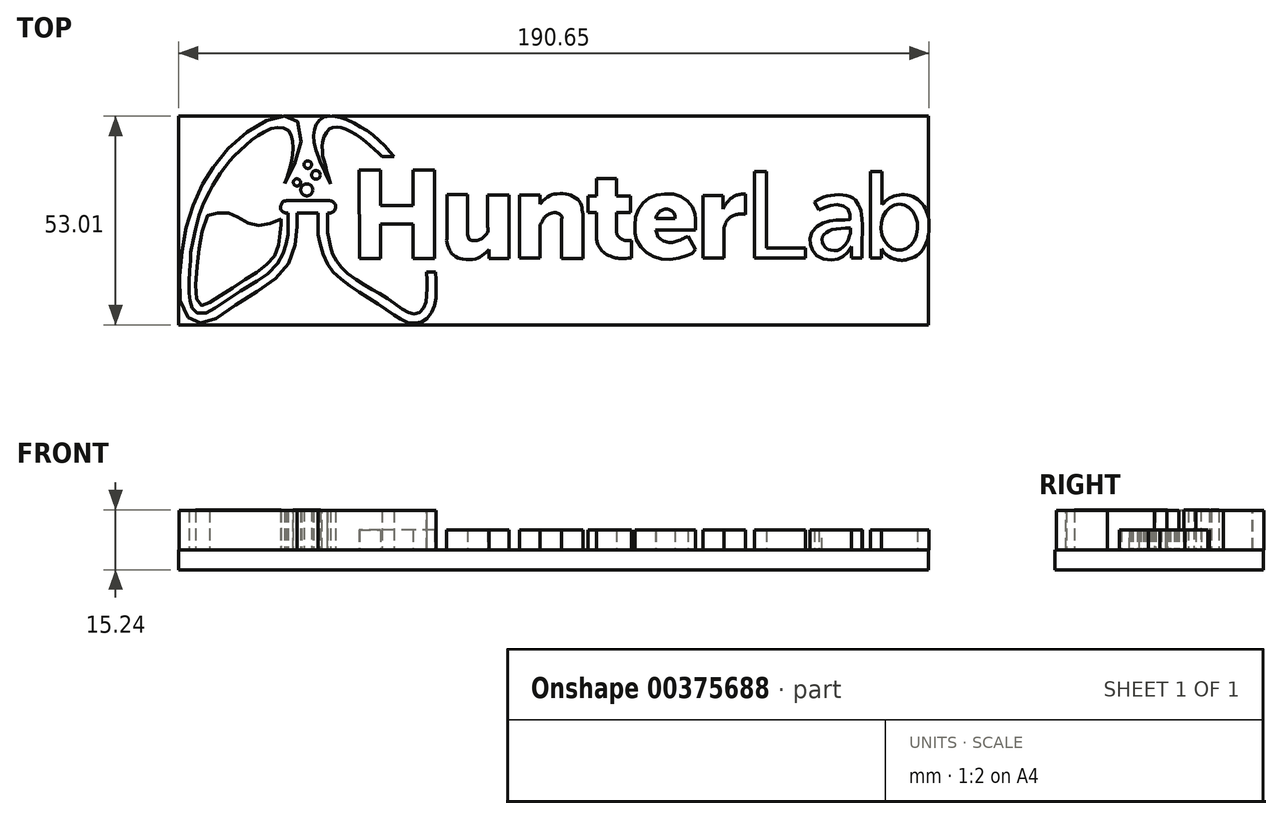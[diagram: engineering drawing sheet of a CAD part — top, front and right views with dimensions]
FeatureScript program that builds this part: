
annotation { "Feature Type Name" : "Feature", "Feature Type Description" : "" }
export const myFeature = defineFeature(function(context is Context, id is Id, definition is map)
    precondition{}
    {
        {
            var Q0;
            Q0=qCreatedBy(makeId("Top.planeOp"),FACE);
            var sketch = newSketch(context, id + "F0", { "sketchPlane" : qUnion([Q0])});
            skLineSegment(sketch, "E0.bottom", {"start": v(-95.8, -13.92) * mm, "end": v(94.76, -13.92) * mm});
            skLineSegment(sketch, "E0.top", {"start": v(-95.8, 39.08) * mm, "end": v(94.76, 39.08) * mm});
            skLineSegment(sketch, "E0.left", {"start": v(-95.8, -13.92) * mm, "end": v(-95.8, 39.08) * mm});
            skLineSegment(sketch, "E0.right", {"start": v(94.76, -13.92) * mm, "end": v(94.76, 39.08) * mm});
            skSolve(sketch);
        }
        {
            var Q0;
            Q0=qSketchRegion(id+"F0",true);
            extrude(context, id + "F1", {"entities" : qUnion([Q0]), "oppositeDirection" : true, "depth" : 5.08 * mm});
        }
        {
            var Q0;
            Q0=qCreatedBy(makeId("Top.planeOp"),FACE);
            var sketch = newSketch(context, id + "F2", { "sketchPlane" : qUnion([Q0])});
            skLineSegment(sketch, "E1", {"start": v(-49.96, 25.38) * mm, "end": v(-44.45, 25.38) * mm});
            skLineSegment(sketch, "E2", {"start": v(-44.45, 25.38) * mm, "end": v(-44.45, 16.38) * mm});
            skLineSegment(sketch, "E3", {"start": v(-44.45, 16.38) * mm, "end": v(-36.19, 16.38) * mm});
            skLineSegment(sketch, "E4", {"start": v(-36.19, 16.38) * mm, "end": v(-36.19, 25.38) * mm});
            skLineSegment(sketch, "E5", {"start": v(-36.19, 25.38) * mm, "end": v(-30.8, 25.38) * mm});
            skLineSegment(sketch, "E6", {"start": v(-30.8, 25.38) * mm, "end": v(-30.8, 2.94) * mm});
            skLineSegment(sketch, "E7", {"start": v(-30.8, 2.94) * mm, "end": v(-36.19, 2.94) * mm});
            skLineSegment(sketch, "E8", {"start": v(-36.19, 2.94) * mm, "end": v(-36.19, 11.68) * mm});
            skLineSegment(sketch, "E9", {"start": v(-36.19, 11.68) * mm, "end": v(-44.45, 11.68) * mm});
            skLineSegment(sketch, "E10", {"start": v(-44.45, 11.68) * mm, "end": v(-44.45, 2.94) * mm});
            skLineSegment(sketch, "E11", {"start": v(-44.45, 2.94) * mm, "end": v(-49.84, 2.94) * mm});
            skLineSegment(sketch, "E12", {"start": v(-49.84, 2.94) * mm, "end": v(-49.96, 25.38) * mm});
            skLineSegment(sketch, "E13", {"start": v(-22.34, 19.15) * mm, "end": v(-27.62, 19.15) * mm});
            skLineSegment(sketch, "E14", {"start": v(-27.62, 19.15) * mm, "end": v(-27.62, 7.97) * mm});
            skLineSegment(sketch, "E15", {"start": v(-22.34, 19.15) * mm, "end": v(-22.34, 9.02) * mm});
            skLineSegment(sketch, "E16", {"start": v(-17.24, 10.98) * mm, "end": v(-17.24, 19.09) * mm});
            skLineSegment(sketch, "E17", {"start": v(-17.24, 19.09) * mm, "end": v(-11.9, 19.09) * mm});
            skLineSegment(sketch, "E18", {"start": v(-11.9, 19.09) * mm, "end": v(-11.9, 2.93) * mm});
            skLineSegment(sketch, "E19", {"start": v(-11.9, 2.93) * mm, "end": v(-16.94, 2.93) * mm});
            skLineSegment(sketch, "E20", {"start": v(-16.94, 2.93) * mm, "end": v(-16.94, 5.2) * mm});
            skLineSegment(sketch, "E21", {"start": v(-3.91, 16.75) * mm, "end": v(-3.91, 19.03) * mm});
            skLineSegment(sketch, "E22", {"start": v(-3.91, 19.03) * mm, "end": v(-9.13, 19.03) * mm});
            skLineSegment(sketch, "E23", {"start": v(-9.13, 19.03) * mm, "end": v(-9.13, 3) * mm});
            skLineSegment(sketch, "E24", {"start": v(-9.13, 3) * mm, "end": v(-3.91, 3) * mm});
            skLineSegment(sketch, "E25", {"start": v(-3.91, 3) * mm, "end": v(-3.91, 11.53) * mm});
            skLineSegment(sketch, "E26", {"start": v(1.55, 12.95) * mm, "end": v(1.55, 2.93) * mm});
            skLineSegment(sketch, "E27", {"start": v(1.55, 2.93) * mm, "end": v(6.9, 2.93) * mm});
            skLineSegment(sketch, "E28", {"start": v(6.9, 2.93) * mm, "end": v(6.9, 14.18) * mm});
            skLineSegment(sketch, "E29", {"start": v(15.5, 9.36) * mm, "end": v(15.5, 14.66) * mm});
            skLineSegment(sketch, "E30", {"start": v(15.5, 14.66) * mm, "end": v(19, 14.66) * mm});
            skLineSegment(sketch, "E31", {"start": v(19, 14.66) * mm, "end": v(19, 18.73) * mm});
            skLineSegment(sketch, "E32", {"start": v(19, 18.73) * mm, "end": v(15.5, 18.73) * mm});
            skLineSegment(sketch, "E33", {"start": v(15.5, 18.73) * mm, "end": v(15.5, 23.29) * mm});
            skLineSegment(sketch, "E34", {"start": v(15.5, 23.29) * mm, "end": v(10.42, 23.29) * mm});
            skLineSegment(sketch, "E35", {"start": v(10.42, 23.29) * mm, "end": v(10.42, 18.73) * mm});
            skLineSegment(sketch, "E36", {"start": v(10.42, 18.73) * mm, "end": v(8.22, 18.73) * mm});
            skLineSegment(sketch, "E37", {"start": v(8.22, 18.73) * mm, "end": v(8.22, 14.66) * mm});
            skLineSegment(sketch, "E38", {"start": v(8.22, 14.66) * mm, "end": v(10.42, 14.66) * mm});
            skLineSegment(sketch, "E39", {"start": v(10.42, 14.66) * mm, "end": v(10.42, 7.8) * mm});
            skLineSegment(sketch, "E40", {"start": v(19.22, 7.53) * mm, "end": v(19.22, 3.01) * mm});
            skLineSegment(sketch, "E41", {"start": v(25.43, 10.11) * mm, "end": v(35.5, 10.11) * mm});
            skLineSegment(sketch, "E42", {"start": v(35.5, 10.11) * mm, "end": v(35.5, 13.01) * mm});
            skLineSegment(sketch, "E43", {"start": v(25.48, 13.06) * mm, "end": v(30.32, 13.06) * mm});
            skLineSegment(sketch, "E44", {"start": v(33.65, 8.61) * mm, "end": v(35.56, 5.18) * mm});
            skLineSegment(sketch, "E45", {"start": v(42.73, 10.52) * mm, "end": v(42.73, 2.99) * mm});
            skLineSegment(sketch, "E46", {"start": v(42.73, 2.99) * mm, "end": v(37.44, 2.99) * mm});
            skLineSegment(sketch, "E47", {"start": v(37.44, 2.99) * mm, "end": v(37.44, 18.97) * mm});
            skLineSegment(sketch, "E48", {"start": v(37.44, 18.97) * mm, "end": v(42.48, 18.97) * mm});
            skLineSegment(sketch, "E49", {"start": v(42.48, 18.97) * mm, "end": v(42.48, 15.46) * mm});
            skLineSegment(sketch, "E50", {"start": v(48.23, 19.32) * mm, "end": v(48.23, 14.13) * mm});
            skLineSegment(sketch, "E51", {"start": v(50.52, 24.97) * mm, "end": v(53.57, 24.97) * mm});
            skLineSegment(sketch, "E52", {"start": v(53.57, 24.97) * mm, "end": v(53.57, 5.64) * mm});
            skLineSegment(sketch, "E53", {"start": v(53.57, 5.64) * mm, "end": v(63.45, 5.64) * mm});
            skLineSegment(sketch, "E54", {"start": v(63.45, 5.64) * mm, "end": v(63.45, 2.99) * mm});
            skLineSegment(sketch, "E55", {"start": v(63.45, 2.99) * mm, "end": v(50.52, 2.99) * mm});
            skLineSegment(sketch, "E56", {"start": v(50.52, 2.99) * mm, "end": v(50.52, 24.97) * mm});
            skLineSegment(sketch, "E57", {"start": v(65.79, 17.29) * mm, "end": v(66.85, 15.2) * mm});
            skLineSegment(sketch, "E58", {"start": v(75.17, 2.99) * mm, "end": v(77.8, 2.99) * mm});
            skLineSegment(sketch, "E59", {"start": v(82.93, 24.97) * mm, "end": v(79.98, 24.97) * mm});
            skLineSegment(sketch, "E60", {"start": v(79.98, 24.97) * mm, "end": v(79.98, 2.99) * mm});
            skLineSegment(sketch, "E61", {"start": v(79.98, 2.99) * mm, "end": v(82.78, 2.99) * mm});
            skLineSegment(sketch, "E62", {"start": v(82.78, 2.99) * mm, "end": v(82.78, 5.28) * mm});
            skLineSegment(sketch, "E63", {"start": v(82.93, 24.97) * mm, "end": v(82.93, 16.58) * mm});
            skFitSpline(sketch, "E64", {"points": [v(82.93, 16.58) * mm, v(84.56, 18.15) * mm, v(86.65, 18.97) * mm, v(89.2, 19.07) * mm, v(91.94, 17.95) * mm, v(93.88, 15.66) * mm, v(94.86, 12.7) * mm, v(94.86, 9.8) * mm, v(94.33, 7.26) * mm, v(92.7, 4.52) * mm, v(91.03, 3.3) * mm, v(88.18, 2.48) * mm, v(85.89, 2.84) * mm, v(84.1, 3.8) * mm, v(82.78, 5.28) * mm], "startDerivative": vector(22.65, 26) * mm, "endDerivative": vector(-19.5, 25.28) * mm});
            skEllipse(sketch, "E65", {"center": v(87.31, 10.88) * mm, "majorRadius": 5.87 * mm, "minorRadius": 4.66 * mm, "majorAxis": v(0, 1)});
            skFitSpline(sketch, "E66", {"points": [v(65.79, 17.29) * mm, v(67.57, 18.3) * mm, v(69.96, 18.97) * mm, v(72.96, 19.07) * mm, v(75.15, 18.46) * mm, v(76.52, 17.29) * mm, v(77.27, 15.83) * mm, v(77.8, 13.58) * mm, v(77.8, 2.99) * mm], "startDerivative": vector(16.24, 10.48) * mm, "endDerivative": vector(-0.09, -55.71) * mm});
            skFitSpline(sketch, "E67", {"points": [v(66.85, 15.2) * mm, v(68.62, 16) * mm, v(70.4, 16.52) * mm, v(72.6, 16.46) * mm, v(74.07, 15.68) * mm, v(74.75, 14.31) * mm, v(74.8, 12.9) * mm, v(74.23, 12.74) * mm, v(71.19, 12.74) * mm, v(68.93, 12.32) * mm, v(66.85, 11.43) * mm, v(65.16, 9.64) * mm, v(64.63, 7.55) * mm, v(64.84, 5.92) * mm, v(65.78, 4.19) * mm, v(68.1, 2.82) * mm, v(70.93, 2.61) * mm, v(72.66, 3.24) * mm, v(73.81, 4.08) * mm, v(75.17, 5.92) * mm], "startDerivative": vector(33.79, 15.82) * mm, "endDerivative": vector(21.23, 32.82) * mm});
            skLineSegment(sketch, "E68", {"start": v(75.17, 5.92) * mm, "end": v(75.17, 2.99) * mm});
            skFitSpline(sketch, "E69", {"points": [v(74.91, 10.64) * mm, v(71.76, 10.48) * mm, v(69.56, 10.01) * mm, v(68.56, 9.33) * mm, v(67.83, 8.54) * mm, v(67.67, 7.34) * mm, v(68.1, 6.29) * mm, v(69.09, 5.34) * mm, v(70.2, 5.03) * mm, v(71.71, 5.03) * mm, v(72.81, 5.66) * mm, v(73.81, 6.65) * mm, v(74.5, 8.02) * mm, v(74.91, 9.33) * mm, v(74.91, 9.28) * mm], "startDerivative": vector(-28.78, -0.8) * mm, "endDerivative": vector(-4.05, -5.26) * mm});
            skLineSegment(sketch, "E70", {"start": v(74.91, 10.64) * mm, "end": v(74.91, 9.33) * mm});
            skFitSpline(sketch, "E71", {"points": [v(42.48, 15.46) * mm, v(43.53, 17.16) * mm, v(44.95, 18.46) * mm, v(46.25, 19.08) * mm, v(48.23, 19.32) * mm], "startDerivative": vector(3.6, 6.76) * mm, "endDerivative": vector(8.08, 0.55) * mm});
            skFitSpline(sketch, "E72", {"points": [v(48.23, 14.13) * mm, v(46.07, 14.13) * mm, v(44.52, 13.5) * mm, v(43.28, 12.14) * mm, v(42.73, 10.52) * mm], "startDerivative": vector(-8.11, 0.9) * mm, "endDerivative": vector(-2.19, -5.73) * mm});
            skFitSpline(sketch, "E73", {"points": [v(35.5, 13.01) * mm, v(35.5, 14) * mm, v(34.49, 16.41) * mm, v(32.63, 18.21) * mm, v(29.9, 19.26) * mm, v(26.62, 19.2) * mm, v(23.71, 18.27) * mm, v(21.73, 16.41) * mm, v(20.3, 13.69) * mm, v(20.12, 10.66) * mm, v(20.37, 8.24) * mm, v(21.8, 5.64) * mm, v(23.96, 3.84) * mm, v(26.87, 2.8) * mm, v(30.28, 2.8) * mm, v(33.62, 3.72) * mm, v(34.61, 4.21) * mm, v(35.56, 5.18) * mm], "startDerivative": vector(2.92, 23.87) * mm, "endDerivative": vector(15.92, 25.8) * mm});
            skFitSpline(sketch, "E74", {"points": [v(33.65, 8.61) * mm, v(32.38, 8) * mm, v(31.02, 7.37) * mm, v(29.84, 7.06) * mm, v(28.3, 7.06) * mm, v(26.93, 7.68) * mm, v(25.94, 8.61) * mm, v(25.43, 10.11) * mm], "startDerivative": vector(-8.12, -5.44) * mm, "endDerivative": vector(-4.59, 9.54) * mm});
            skFitSpline(sketch, "E75", {"points": [v(15.5, 9.36) * mm, v(15.79, 8.67) * mm, v(16.73, 7.86) * mm, v(17.84, 7.5) * mm, v(19.22, 7.53) * mm], "startDerivative": vector(0.88, -3.35) * mm, "endDerivative": vector(5.13, 0.44) * mm});
            skFitSpline(sketch, "E76", {"points": [v(10.42, 7.8) * mm, v(10.62, 6.68) * mm, v(11.4, 5.33) * mm, v(12.66, 4.15) * mm, v(14.64, 3.27) * mm, v(16.09, 2.98) * mm, v(19.22, 3.01) * mm], "startDerivative": vector(0.64, -8.95) * mm, "endDerivative": vector(16.04, 0.67) * mm});
            skFitSpline(sketch, "E77", {"points": [v(-3.91, 16.75) * mm, v(-3.07, 17.74) * mm, v(-1.3, 18.95) * mm, v(0, 19.3) * mm, v(2.44, 19.35) * mm, v(3.95, 18.95) * mm, v(5.72, 17.79) * mm, v(6.42, 16.75) * mm, v(6.73, 15.42) * mm, v(6.9, 14.18) * mm], "startDerivative": vector(7.09, 9.57) * mm, "endDerivative": vector(1.61, -12.4) * mm});
            skFitSpline(sketch, "E78", {"points": [v(1.55, 12.95) * mm, v(1.55, 13.65) * mm, v(1.02, 14.18) * mm, v(0, 14.6) * mm, v(-1.75, 14.18) * mm, v(-2.56, 13.65) * mm, v(-3.12, 12.95) * mm, v(-3.42, 12.24) * mm, v(-3.91, 11.53) * mm], "startDerivative": vector(1.14, 7.02) * mm, "endDerivative": vector(-4.71, -5.81) * mm});
            skFitSpline(sketch, "E79", {"points": [v(-17.24, 10.98) * mm, v(-17.24, 9.86) * mm, v(-18.25, 8.41) * mm, v(-19.13, 7.8) * mm, v(-20.35, 7.46) * mm, v(-21.23, 7.5) * mm, v(-21.92, 7.8) * mm, v(-22.34, 9.02) * mm], "startDerivative": vector(1.28, -7.5) * mm, "endDerivative": vector(-1.92, 8.98) * mm});
            skFitSpline(sketch, "E80", {"points": [v(-27.62, 7.97) * mm, v(-27.62, 6.84) * mm, v(-27, 5.23) * mm, v(-26.42, 4.25) * mm, v(-25.07, 3.2) * mm, v(-23.4, 2.77) * mm, v(-20.58, 2.77) * mm, v(-19.03, 3.4) * mm, v(-17.72, 4.44) * mm, v(-16.94, 5.2) * mm], "startDerivative": vector(-1.32, -11.42) * mm, "endDerivative": vector(7.85, 7.93) * mm});
            skFitSpline(sketch, "E81", {"points": [v(25.48, 13.06) * mm, v(25.72, 13.85) * mm, v(26.5, 14.87) * mm, v(27.26, 15.33) * mm, v(28.05, 15.46) * mm, v(28.92, 15.35) * mm, v(29.6, 14.95) * mm, v(30.16, 14.22) * mm, v(30.32, 13.56) * mm, v(30.32, 13.06) * mm], "startDerivative": vector(1.4, 6.81) * mm, "endDerivative": vector(-0.2, -5.58) * mm});
            skLineSegment(sketch, "E82.bottom", {"start": v(-95.64, 39.01) * mm, "end": v(94.86, 39.01) * mm});
            skLineSegment(sketch, "E82.top", {"start": v(-95.64, -13.6) * mm, "end": v(94.86, -13.6) * mm});
            skLineSegment(sketch, "E82.left", {"start": v(-95.64, 39.01) * mm, "end": v(-95.64, -13.6) * mm});
            skLineSegment(sketch, "E82.right", {"start": v(94.86, 39.01) * mm, "end": v(94.86, -13.6) * mm});
            skSolve(sketch);
        }
        {
            var Q0;
            Q0=makeQuery(id+"F2.imprint","IMPRINT",FACE,{"disambiguationData":[TD([[makeQuery(id+"F2.imprint","IMPRINT",EDGE,{"derivedFrom":sQuery(id+"F2.wireOp",EDGE,"E1")}),-1.0]])]});
            var Q1;
            Q1=makeQuery(id+"F2.imprint","IMPRINT",FACE,{"disambiguationData":[TD([[makeQuery(id+"F2.imprint","IMPRINT",EDGE,{"derivedFrom":sQuery(id+"F2.wireOp",EDGE,"E13")}),1.0]])]});
            var Q2;
            Q2=makeQuery(id+"F2.imprint","IMPRINT",FACE,{"disambiguationData":[TD([[makeQuery(id+"F2.imprint","IMPRINT",EDGE,{"derivedFrom":sQuery(id+"F2.wireOp",EDGE,"E21")}),1.0]])]});
            var Q3;
            Q3=makeQuery(id+"F2.imprint","IMPRINT",FACE,{"disambiguationData":[TD([[makeQuery(id+"F2.imprint","IMPRINT",EDGE,{"derivedFrom":sQuery(id+"F2.wireOp",EDGE,"E29")}),1.0]])]});
            var Q4;
            Q4=makeQuery(id+"F2.imprint","IMPRINT",FACE,{"disambiguationData":[TD([[makeQuery(id+"F2.imprint","IMPRINT",EDGE,{"derivedFrom":sQuery(id+"F2.wireOp",EDGE,"E45")}),-1.0]])]});
            var Q5;
            Q5=makeQuery(id+"F2.imprint","IMPRINT",FACE,{"disambiguationData":[TD([[makeQuery(id+"F2.imprint","IMPRINT",EDGE,{"derivedFrom":sQuery(id+"F2.wireOp",EDGE,"E41")}),1.0]])]});
            extrude(context, id + "F3", {"entities" : qUnion([Q0, Q1, Q2, Q3, Q4, Q5]), "operationType" : NewBodyOperationType.ADD, "depth" : 5 * mm, "offsetDistance" : 25.4 * mm});
        }
        {
            var Q0;
            Q0=makeQuery(id+"F2.imprint","IMPRINT",FACE,{"disambiguationData":[TD([[makeQuery(id+"F2.imprint","IMPRINT",EDGE,{"derivedFrom":sQuery(id+"F2.wireOp",EDGE,"E51")}),-1.0]])]});
            var Q1;
            Q1=makeQuery(id+"F2.imprint","IMPRINT",FACE,{"disambiguationData":[TD([[makeQuery(id+"F2.imprint","IMPRINT",EDGE,{"derivedFrom":sQuery(id+"F2.wireOp",EDGE,"E57")}),1.0]])]});
            var Q2;
            Q2=makeQuery(id+"F2.imprint","IMPRINT",FACE,{"disambiguationData":[TD([[makeQuery(id+"F2.imprint","IMPRINT",EDGE,{"derivedFrom":sQuery(id+"F2.wireOp",EDGE,"E59")}),1.0]])]});
            extrude(context, id + "F4", {"entities" : qUnion([Q0, Q1, Q2]), "operationType" : NewBodyOperationType.ADD, "depth" : 5 * mm, "offsetDistance" : 25.4 * mm});
        }
        {
            var Q0;
            Q0=makeQuery(id+"F2.imprint","IMPRINT",FACE,{"disambiguationData":[TD([[makeQuery(id+"F2.imprint","IMPRINT",EDGE,{"derivedFrom":sQuery(id+"F2.wireOp",EDGE,"E1")}),1.0]])]});
            var sketch = newSketch(context, id + "F5", { "sketchPlane" : qUnion([Q0])});
            skLineSegment(sketch, "E83", {"start": v(-68.34, 17.61) * mm, "end": v(-58.06, 17.61) * mm});
            skLineSegment(sketch, "E84", {"start": v(-67.95, 14.5) * mm, "end": v(-67.95, 11.06) * mm});
            skLineSegment(sketch, "E85", {"start": v(-57.94, 14.5) * mm, "end": v(-57.94, 11.36) * mm});
            skLineSegment(sketch, "E86", {"start": v(-65.7, 11.06) * mm, "end": v(-65.7, 14.5) * mm});
            skLineSegment(sketch, "E87", {"start": v(-65.7, 14.5) * mm, "end": v(-60.32, 14.5) * mm});
            skLineSegment(sketch, "E88", {"start": v(-60.32, 14.5) * mm, "end": v(-60.32, 11.26) * mm});
            skFitSpline(sketch, "E89", {"points": [v(-68.34, 17.61) * mm, v(-69.09, 17.46) * mm, v(-69.64, 16.83) * mm, v(-69.86, 16.05) * mm, v(-69.83, 15.46) * mm, v(-69.42, 14.87) * mm, v(-68.72, 14.54) * mm, v(-67.95, 14.5) * mm], "startDerivative": vector(-5.2, -2.07) * mm, "endDerivative": vector(5.37, 0.05) * mm});
            skFitSpline(sketch, "E90", {"points": [v(-57.94, 14.5) * mm, v(-57.16, 14.5) * mm, v(-56.52, 14.8) * mm, v(-56.05, 15.33) * mm, v(-55.97, 16.62) * mm, v(-56.3, 17.09) * mm, v(-56.85, 17.45) * mm, v(-57.46, 17.61) * mm, v(-58.06, 17.61) * mm], "startDerivative": vector(6.89, -0.67) * mm, "endDerivative": vector(-5.35, -0.27) * mm});
            skFitSpline(sketch, "E91", {"points": [v(-67.95, 11.06) * mm, v(-67.95, 9.88) * mm, v(-68.13, 8.36) * mm, v(-68.56, 6.34) * mm, v(-69.12, 4.33) * mm, v(-70.12, 2.36) * mm, v(-73.05, -0.87) * mm, v(-75.55, -2.54) * mm, v(-81.55, -6.33) * mm, v(-85.1, -8.77) * mm, v(-88.16, -10.69) * mm, v(-89.3, -11) * mm, v(-90.94, -11) * mm, v(-91.74, -10.41) * mm, v(-92.4, -9.55) * mm, v(-92.76, -8.43) * mm, v(-92.92, -7.3) * mm, v(-93.07, -5.84) * mm, v(-93.1, -3.37) * mm, v(-93.07, -0.96) * mm, v(-92.86, 1.6) * mm, v(-92.76, 2.96) * mm, v(-92.7, 4.23) * mm, v(-92.2, 7.2) * mm, v(-91.68, 9.64) * mm, v(-90.57, 13.87) * mm, v(-89.49, 16.8) * mm, v(-87.96, 19.99) * mm], "startDerivative": vector(1.14, -43.6) * mm, "endDerivative": vector(35.58, 72.1) * mm});
            skFitSpline(sketch, "E92", {"points": [v(-68.93, 21.94) * mm, v(-67.66, 23.8) * mm, v(-66.4, 26.83) * mm, v(-65.53, 29.23) * mm, v(-64.67, 32.63) * mm, v(-64.67, 35.3) * mm, v(-65.3, 37.39) * mm, v(-66.53, 38.52) * mm, v(-67.48, 38.93) * mm, v(-68.16, 39.02) * mm, v(-69.88, 39.06) * mm, v(-71.55, 38.6) * mm, v(-73.64, 37.84) * mm, v(-75.9, 36.7) * mm, v(-78.53, 34.94) * mm, v(-81.16, 32.81) * mm, v(-83.7, 30.23) * mm, v(-85.73, 27.87) * mm, v(-87.5, 25.43) * mm, v(-88.18, 24.34) * mm, v(-89.67, 21.94) * mm, v(-90.76, 19.63) * mm, v(-92.12, 16.5) * mm, v(-93.25, 13.15) * mm, v(-93.88, 10.7) * mm, v(-94.56, 7.63) * mm, v(-94.97, 4.5) * mm, v(-95.33, 0.75) * mm, v(-95.56, -2.97) * mm, v(-95.56, -6.73) * mm, v(-95.33, -8.36) * mm, v(-94.65, -10.67) * mm, v(-93.34, -12.12) * mm, v(-92.61, -12.75) * mm, v(-91.53, -13.25) * mm, v(-90.67, -13.39) * mm, v(-89.4, -13.43) * mm, v(-88.08, -13.11) * mm, v(-86.54, -12.43) * mm, v(-83.83, -10.85) * mm, v(-81.47, -9.04) * mm, v(-78.08, -6.9) * mm, v(-75.45, -5.2) * mm, v(-73, -3.6) * mm, v(-70.87, -1.93) * mm, v(-69.42, -0.57) * mm, v(-68.16, 1.1) * mm, v(-67.07, 3.42) * mm, v(-66.53, 5.23) * mm, v(-66.03, 7.13) * mm, v(-65.8, 8.67) * mm, v(-65.7, 11.06) * mm], "startDerivative": vector(68.15, 87.24) * mm, "endDerivative": vector(3.62, 129.17) * mm});
            skFitSpline(sketch, "E93", {"points": [v(-60.32, 11.26) * mm, v(-60.32, 8.96) * mm, v(-59.76, 6.3) * mm, v(-58.55, 2.66) * mm, v(-57.04, 0) * mm, v(-54.73, -2.14) * mm, v(-51.7, -4.45) * mm, v(-48.6, -6.38) * mm, v(-45.34, -8.5) * mm, v(-42.84, -10.2) * mm, v(-40.69, -11.68) * mm, v(-39.36, -12.48) * mm, v(-37.58, -13.3) * mm, v(-36.45, -13.46) * mm, v(-34.82, -13.46) * mm, v(-33.42, -12.9) * mm, v(-32.36, -11.95) * mm, v(-31.3, -10.47) * mm, v(-30.7, -8.96) * mm, v(-30.43, -7.25) * mm, v(-30.4, -5.28) * mm, v(-30.4, -2.48) * mm, v(-30.46, -0.56) * mm], "startDerivative": vector(-2.67, -49.82) * mm, "endDerivative": vector(-2.24, 43.27) * mm});
            skFitSpline(sketch, "E94", {"points": [v(-57.94, 11.36) * mm, v(-57.94, 9.63) * mm, v(-57.64, 8.06) * mm, v(-57.29, 6.06) * mm, v(-56.82, 4.31) * mm, v(-55.78, 2.42) * mm, v(-54.43, 0.63) * mm, v(-52.85, -0.87) * mm, v(-49.78, -2.98) * mm, v(-47.35, -4.48) * mm, v(-45.28, -5.7) * mm, v(-42.84, -7.13) * mm, v(-40.83, -8.6) * mm, v(-38.54, -10.18) * mm, v(-37.1, -10.93) * mm, v(-36, -11.11) * mm, v(-34.93, -11.07) * mm, v(-34.1, -10.38) * mm, v(-33.32, -9.32) * mm, v(-32.82, -7.95) * mm, v(-32.75, -6.5) * mm, v(-32.72, -4.67) * mm, v(-32.71, -2.8) * mm, v(-32.81, -0.56) * mm], "startDerivative": vector(-2, -43.26) * mm, "endDerivative": vector(-2.63, 49.7) * mm});
            skLineSegment(sketch, "E95", {"start": v(-32.81, -0.56) * mm, "end": v(-30.46, -0.56) * mm});
            skLineSegment(sketch, "E96", {"start": v(-44.1, 28.8) * mm, "end": v(-41.04, 28.8) * mm});
            skFitSpline(sketch, "E97", {"points": [v(-41.04, 28.8) * mm, v(-43.35, 31.44) * mm, v(-46.9, 34.61) * mm, v(-50.23, 36.77) * mm, v(-54, 38.54) * mm, v(-56.1, 39.03) * mm, v(-58.46, 38.92) * mm, v(-60.34, 37.68) * mm, v(-61.26, 35.8) * mm, v(-61.42, 32.84) * mm, v(-60.34, 28.8) * mm, v(-59.22, 26.28) * mm, v(-57.23, 21.87) * mm], "startDerivative": vector(-24.59, 29.7) * mm, "endDerivative": vector(21.06, -47.4) * mm});
            skFitSpline(sketch, "E98", {"points": [v(-44.1, 28.8) * mm, v(-45.4, 30.04) * mm, v(-47.17, 31.66) * mm, v(-49.1, 33.27) * mm, v(-51.3, 34.78) * mm, v(-53.4, 35.8) * mm, v(-54.8, 36.23) * mm, v(-56.1, 36.28) * mm, v(-57.17, 36.01) * mm, v(-58.09, 35.2) * mm, v(-58.9, 33.75) * mm, v(-59.27, 31.76) * mm, v(-59.27, 30.37) * mm, v(-59.1, 28.8) * mm, v(-58.66, 27.23) * mm, v(-58.11, 25) * mm, v(-57.23, 21.87) * mm], "startDerivative": vector(-20.2, 19.59) * mm, "endDerivative": vector(11.71, -39.23) * mm});
            skFitSpline(sketch, "E99", {"points": [v(-68.93, 21.94) * mm, v(-68.16, 23.8) * mm, v(-67.3, 26.8) * mm, v(-66.87, 28.96) * mm, v(-66.66, 30.64) * mm, v(-66.78, 32.63) * mm, v(-67.15, 34.16) * mm, v(-67.66, 35.32) * mm, v(-68.93, 36.05) * mm, v(-70.27, 36.24) * mm, v(-72.1, 35.96) * mm, v(-74.11, 35.01) * mm, v(-76.07, 33.85) * mm, v(-78.06, 32.26) * mm, v(-79.86, 30.7) * mm, v(-81.81, 28.75) * mm, v(-83.04, 27.44) * mm, v(-84.65, 25.24) * mm, v(-86.15, 23.13) * mm, v(-87.13, 21.54) * mm, v(-87.96, 19.99) * mm], "startDerivative": vector(15.55, 34.4) * mm, "endDerivative": vector(-17.61, -33.71) * mm});
            skSolve(sketch);
        }
        {
            var Q0;
            Q0=qSketchRegion(id+"F5",true);
            extrude(context, id + "F6", {"entities" : qUnion([Q0]), "depth" : 10 * mm, "offsetDistance" : 25.4 * mm});
        }
        {
            var Q0;
            Q0=makeQuery(id+"F2.imprint","IMPRINT",FACE,{"disambiguationData":[TD([[makeQuery(id+"F2.imprint","IMPRINT",EDGE,{"derivedFrom":sQuery(id+"F2.wireOp",EDGE,"E1")}),1.0]])]});
            var sketch = newSketch(context, id + "F7", { "sketchPlane" : qUnion([Q0])});
            skCircle(sketch, "E100", {"center": v(-63.22, 20.36) * mm, "radius": 1.54 * mm});
            skCircle(sketch, "E101", {"center": v(-60.88, 24.17) * mm, "radius": 1.1 * mm});
            skCircle(sketch, "E102", {"center": v(-65.73, 22.27) * mm, "radius": 0.92 * mm});
            skCircle(sketch, "E103", {"center": v(-62.96, 26.76) * mm, "radius": 0.97 * mm});
            skFitSpline(sketch, "E104", {"points": [v(-69.7, 12.93) * mm, v(-72.12, 11.98) * mm, v(-73.85, 11.55) * mm, v(-76.19, 11.37) * mm, v(-77.92, 11.9) * mm, v(-80, 13.02) * mm, v(-81.9, 14.05) * mm, v(-83.19, 14.49) * mm, v(-85.18, 14.57) * mm, v(-87.17, 14.14) * mm, v(-88.64, 13.62) * mm, v(-90.02, 8.52) * mm, v(-90.8, 4.03) * mm, v(-91.32, -1.77) * mm, v(-91.4, -6.18) * mm, v(-90.88, -8.16) * mm, v(-90.36, -8.86) * mm, v(-89.3, -9) * mm, v(-88.11, -8.41) * mm, v(-85.96, -7) * mm, v(-83.3, -5.37) * mm, v(-80.18, -3.22) * mm, v(-77.28, -1.44) * mm, v(-75.2, 0) * mm, v(-73.13, 1.6) * mm, v(-71.65, 3.24) * mm, v(-70.6, 5.46) * mm, v(-70.24, 7.32) * mm, v(-69.94, 9.91) * mm, v(-69.8, 11.46) * mm, v(-69.8, 11.6) * mm], "startDerivative": vector(-66.54, -31.72) * mm, "endDerivative": vector(0, -39.97) * mm});
            skLineSegment(sketch, "E105", {"start": v(-69.7, 12.93) * mm, "end": v(-69.8, 11.72) * mm});
            skLineSegment(sketch, "E106", {"start": v(-69.8, 11.72) * mm, "end": v(-69.8, 11.6) * mm});
            skSolve(sketch);
        }
        {
            var Q0;
            Q0=makeQuery(id+"F7.imprint","IMPRINT",FACE,{"disambiguationData":[TD([[makeQuery(id+"F7.imprint","IMPRINT",EDGE,{"derivedFrom":sQuery(id+"F7.wireOp",EDGE,"E102")}),1.0]])]});
            var Q1;
            Q1=makeQuery(id+"F7.imprint","IMPRINT",FACE,{"disambiguationData":[TD([[makeQuery(id+"F7.imprint","IMPRINT",EDGE,{"derivedFrom":sQuery(id+"F7.wireOp",EDGE,"E100")}),1.0]])]});
            var Q2;
            Q2=makeQuery(id+"F7.imprint","IMPRINT",FACE,{"disambiguationData":[TD([[makeQuery(id+"F7.imprint","IMPRINT",EDGE,{"derivedFrom":sQuery(id+"F7.wireOp",EDGE,"E101")}),1.0]])]});
            var Q3;
            Q3=makeQuery(id+"F7.imprint","IMPRINT",FACE,{"disambiguationData":[TD([[makeQuery(id+"F7.imprint","IMPRINT",EDGE,{"derivedFrom":sQuery(id+"F7.wireOp",EDGE,"E103")}),1.0]])]});
            var Q4;
            Q4=makeQuery(id+"F7.imprint","IMPRINT",FACE,{"disambiguationData":[TD([[makeQuery(id+"F7.imprint","IMPRINT",EDGE,{"derivedFrom":sQuery(id+"F7.wireOp",EDGE,"E104")}),1.0]])]});
            extrude(context, id + "F8", {"entities" : qUnion([Q0, Q1, Q2, Q3, Q4]), "operationType" : NewBodyOperationType.ADD, "depth" : 10.16 * mm});
        }
    });
